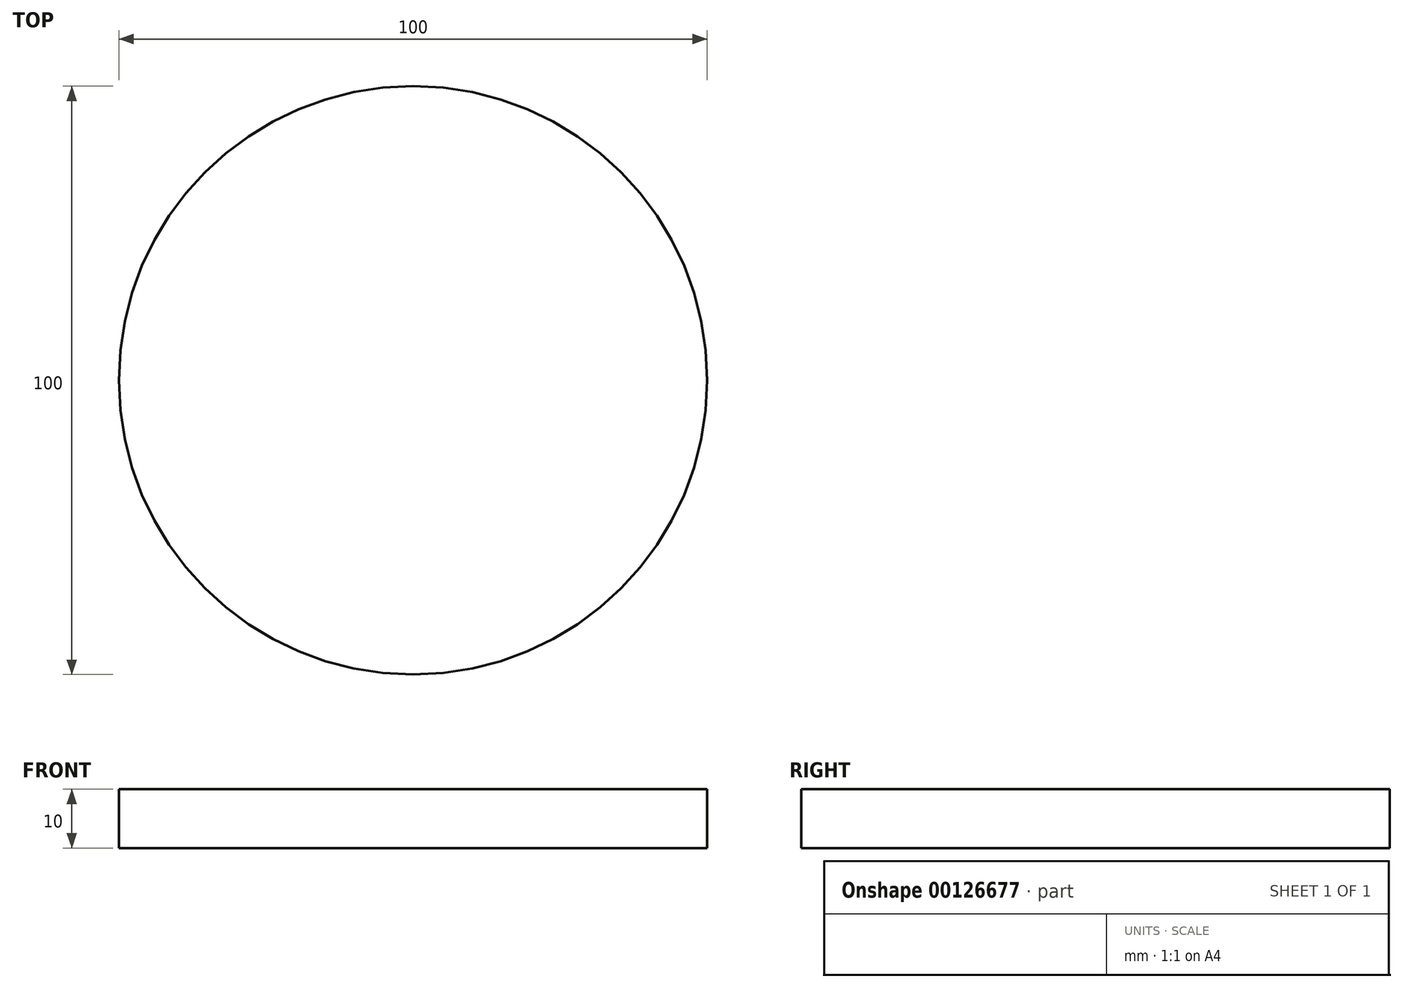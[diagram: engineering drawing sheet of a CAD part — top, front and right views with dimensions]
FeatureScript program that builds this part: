
annotation { "Feature Type Name" : "Feature", "Feature Type Description" : "" }
export const myFeature = defineFeature(function(context is Context, id is Id, definition is map)
    precondition{}
    {
        {
            var Q0;
            Q0=qCreatedBy(makeId("Top.planeOp"),FACE);
            var sketch = newSketch(context, id + "F0", { "sketchPlane" : qUnion([Q0])});
            skCircle(sketch, "E0", {"center": v(0, 0) * mm, "radius": 50 * mm});
            skSolve(sketch);
        }
        {
            var Q0;
            Q0 = qSketchRegion(id + "F0", true);
            extrude(context, id + "F1", {"entities" : qUnion([Q0]), "depth" : 10 * mm});
        }
    });
